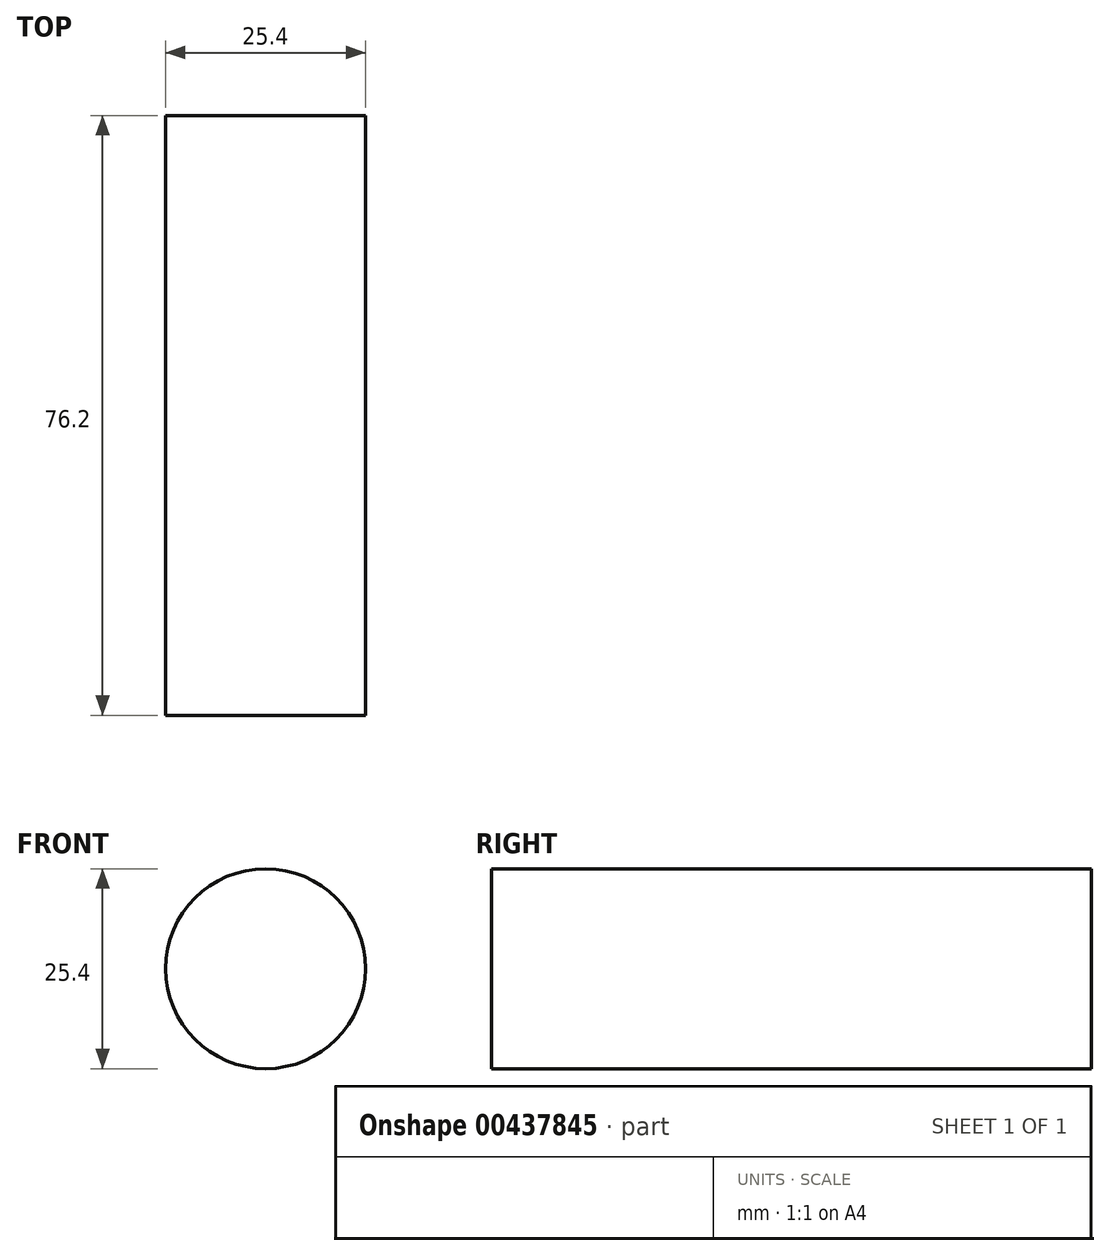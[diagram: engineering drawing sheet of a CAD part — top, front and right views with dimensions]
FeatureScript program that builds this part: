
annotation { "Feature Type Name" : "Feature", "Feature Type Description" : "" }
export const myFeature = defineFeature(function(context is Context, id is Id, definition is map)
    precondition{}
    {
        {
            var Q0;
            Q0=qCreatedBy(makeId("Front.planeOp"),FACE);
            var sketch = newSketch(context, id + "F0", { "sketchPlane" : qUnion([Q0])});
            skCircle(sketch, "E0", {"center": v(-43.73, 40.67) * mm, "radius": 12.7 * mm});
            skSolve(sketch);
        }
        {
            var Q0;
            Q0 = qSketchRegion(id + "F0", true);
            extrude(context, id + "F1", {"entities" : qUnion([Q0]), "depth" : 76.2 * mm});
        }
    });
